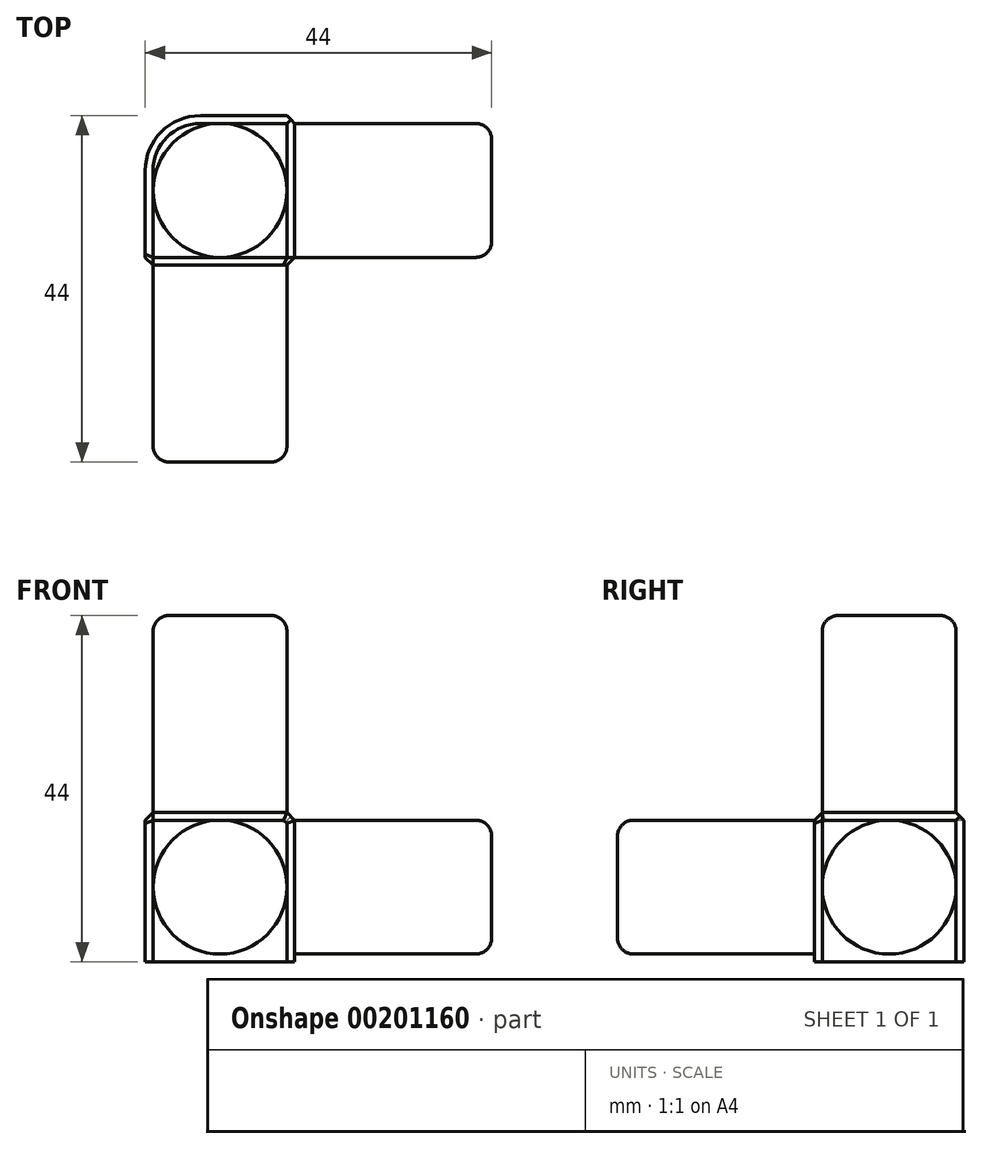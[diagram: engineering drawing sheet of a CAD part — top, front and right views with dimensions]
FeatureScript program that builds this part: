
annotation { "Feature Type Name" : "Feature", "Feature Type Description" : "" }
export const myFeature = defineFeature(function(context is Context, id is Id, definition is map)
    precondition{}
    {
        {
            var Q0;
            Q0=qCreatedBy(makeId("Top.planeOp"),FACE);
            var sketch = newSketch(context, id + "F0", { "sketchPlane" : qUnion([Q0])});
            skLineSegment(sketch, "E0.bottom", {"start": v(-14.38, 5.37) * mm, "end": v(4.62, 5.37) * mm});
            skLineSegment(sketch, "E0.top", {"start": v(-14.38, -13.63) * mm, "end": v(4.62, -13.63) * mm});
            skLineSegment(sketch, "E0.left", {"start": v(-14.38, 5.37) * mm, "end": v(-14.38, -13.63) * mm});
            skLineSegment(sketch, "E0.right", {"start": v(4.62, 5.37) * mm, "end": v(4.62, -13.63) * mm});
            skSolve(sketch);
        }
        {
            var Q0;
            Q0 = qSketchRegion(id + "F0", true);
            extrude(context, id + "F1", {"entities" : qUnion([Q0]), "depth" : 19 * mm});
        }
        {
            var Q0;
            Q0=makeQuery(id+"F1.opExtrude","SWEPT_FACE",FACE,{"disambiguationData":[OSD([sQuery(id+"F0.wireOp",EDGE,"E0.top")])]});
            var sketch = newSketch(context, id + "F2", { "sketchPlane" : qUnion([Q0])});
            skCircle(sketch, "E1", {"center": v(-4.88, 9.5) * mm, "radius": 8.5 * mm});
            skPoint(sketch, "E1.centerSnap0", {"position": v(4.62, 9.5) * mm});
            skPoint(sketch, "E1.centerSnap1", {"position": v(-4.88, 0) * mm});
            skSolve(sketch);
        }
        {
            var Q0;
            Q0=makeQuery(id+"F1.opExtrude","SWEPT_FACE",FACE,{"disambiguationData":[OSD([sQuery(id+"F0.wireOp",EDGE,"E0.right")])]});
            var sketch = newSketch(context, id + "F3", { "sketchPlane" : qUnion([Q0])});
            skCircle(sketch, "E2", {"center": v(-4.13, 9.5) * mm, "radius": 8.5 * mm});
            skPoint(sketch, "E2.centerSnap0", {"position": v(5.37, 9.5) * mm});
            skPoint(sketch, "E2.centerSnap1", {"position": v(-4.13, 0) * mm});
            skSolve(sketch);
        }
        {
            var Q0;
            Q0=makeQuery(id+"F1.opExtrude","CAP_FACE",FACE,{"disambiguationData":[OSD([sQuery(id+"F0.wireOp",EDGE,"E0.bottom"),sQuery(id+"F0.wireOp",EDGE,"E0.top"),sQuery(id+"F0.wireOp",EDGE,"E0.left"),sQuery(id+"F0.wireOp",EDGE,"E0.right")])],"isStart":false});
            var sketch = newSketch(context, id + "F4", { "sketchPlane" : qUnion([Q0])});
            skCircle(sketch, "E3", {"center": v(-4.88, -4.13) * mm, "radius": 8.5 * mm});
            skPoint(sketch, "E3.centerSnap0", {"position": v(-4.88, -13.63) * mm});
            skPoint(sketch, "E3.centerSnap1", {"position": v(-14.38, -4.13) * mm});
            skSolve(sketch);
        }
        {
            var Q0;
            Q0=makeQuery(id+"F2.imprint","IMPRINT",FACE,{"disambiguationData":[TD([[makeQuery(id+"F2.imprint","IMPRINT",EDGE,{"derivedFrom":sQuery(id+"F2.wireOp",EDGE,"E1")}),1.0]])]});
            extrude(context, id + "F5", {"entities" : qUnion([Q0]), "operationType" : NewBodyOperationType.ADD, "depth" : 25 * mm});
        }
        {
            var Q0;
            Q0=makeQuery(id+"F3.imprint","IMPRINT",FACE,{"disambiguationData":[TD([[makeQuery(id+"F3.imprint","IMPRINT",EDGE,{"derivedFrom":sQuery(id+"F3.wireOp",EDGE,"E2")}),1.0]])]});
            extrude(context, id + "F6", {"entities" : qUnion([Q0]), "operationType" : NewBodyOperationType.ADD, "depth" : 25 * mm});
        }
        {
            var Q0;
            Q0=makeQuery(id+"F4.imprint","IMPRINT",FACE,{"disambiguationData":[TD([[makeQuery(id+"F4.imprint","IMPRINT",EDGE,{"derivedFrom":sQuery(id+"F4.wireOp",EDGE,"E3")}),1.0]])]});
            extrude(context, id + "F7", {"entities" : qUnion([Q0]), "operationType" : NewBodyOperationType.ADD, "depth" : 25 * mm});
        }
        {
            var Q0;
            Q0=makeQuery(id+"F5.opExtrude","CAP_EDGE",EDGE,{"disambiguationData":[OSD([sQuery(id+"F2.wireOp",EDGE,"E1")])],"isStart":false});
            var Q1;
            Q1=makeQuery(id+"F6.opExtrude","CAP_EDGE",EDGE,{"disambiguationData":[OSD([sQuery(id+"F3.wireOp",EDGE,"E2")])],"isStart":false});
            var Q2;
            Q2=makeQuery(id+"F7.opExtrude","CAP_EDGE",EDGE,{"disambiguationData":[OSD([sQuery(id+"F4.wireOp",EDGE,"E3")])],"isStart":false});
            fillet(context, id + "F8", {"entities" : qUnion([Q0, Q1, Q2]), "radius" : 2 * mm, "tangentPropagation" : true, "allowEdgeOverflow" : false});
        }
        {
            var Q0;
            Q0=makeQuery(id+"F1.opExtrude","SWEPT_EDGE",EDGE,{"disambiguationData":[OSD([sQuery(id+"F0.wireOp",EDGE,"E0.bottom"),sQuery(id+"F0.wireOp",EDGE,"E0.left")])]});
            fillet(context, id + "F9", {"entities" : qUnion([Q0]), "radius" : 7 * mm, "tangentPropagation" : true, "allowEdgeOverflow" : false});
        }
        {
            var Q0;
            Q0=makeQuery(id+"F1.opExtrude","CAP_EDGE",EDGE,{"disambiguationData":[OSD([sQuery(id+"F0.wireOp",EDGE,"E0.right")])],"isStart":false});
            chamfer(context, id + "F10", {"entities" : qUnion([Q0]), "width" : 1 * mm, "tangentPropagation" : true});
        }
        {
            var Q0;
            Q0=makeQuery(id+"F1.opExtrude","SWEPT_EDGE",EDGE,{"disambiguationData":[OSD([sQuery(id+"F0.wireOp",EDGE,"E0.top"),sQuery(id+"F0.wireOp",EDGE,"E0.right")])]});
            var Q1;
            Q1=makeQuery(id+"F10.opChamfer","BLEND_EDGE",EDGE,{"blendedFrom":[makeQuery(id+"F1.opExtrude","CAP_EDGE",EDGE,{"disambiguationData":[OSD([sQuery(id+"F0.wireOp",EDGE,"E0.right")])],"isStart":false}),makeQuery(id+"F1.opExtrude","SWEPT_FACE",FACE,{"disambiguationData":[OSD([sQuery(id+"F0.wireOp",EDGE,"E0.top")])]})],"blendedInto":[makeQuery(id+"F1.opExtrude","SWEPT_FACE",FACE,{"disambiguationData":[OSD([sQuery(id+"F0.wireOp",EDGE,"E0.top")])]})]});
            var Q2;
            Q2=makeQuery(id+"F1.opExtrude","CAP_EDGE",EDGE,{"disambiguationData":[OSD([sQuery(id+"F0.wireOp",EDGE,"E0.top")])],"isStart":false});
            chamfer(context, id + "F11", {"entities" : qUnion([Q0, Q1, Q2]), "width" : 1 * mm, "tangentPropagation" : true});
        }
        {
            var Q0;
            Q0=makeQuery(id+"F1.opExtrude","CAP_EDGE",EDGE,{"disambiguationData":[OSD([sQuery(id+"F0.wireOp",EDGE,"E0.bottom")])],"isStart":false});
            var Q1;
            {var subQ0=sQuery(id+"F0.wireOp",EDGE,"E0.left");var subQ1=sQuery(id+"F0.wireOp",EDGE,"E0.bottom");Q1=makeQuery(id+"F9.opFillet","BLEND_EDGE",EDGE,{"blendedFrom":[makeQuery(id+"F1.opExtrude","SWEPT_EDGE",EDGE,{"disambiguationData":[OSD([subQ1,subQ0])]}),makeQuery(id+"F1.opExtrude","CAP_FACE",FACE,{"disambiguationData":[OSD([subQ1,sQuery(id+"F0.wireOp",EDGE,"E0.top"),subQ0,sQuery(id+"F0.wireOp",EDGE,"E0.right")])],"isStart":false})],"blendedInto":[makeQuery(id+"F1.opExtrude","CAP_FACE",FACE,{"disambiguationData":[OSD([subQ1,sQuery(id+"F0.wireOp",EDGE,"E0.top"),subQ0,sQuery(id+"F0.wireOp",EDGE,"E0.right")])],"isStart":false})]});}
            var Q2;
            Q2=makeQuery(id+"F1.opExtrude","CAP_EDGE",EDGE,{"disambiguationData":[OSD([sQuery(id+"F0.wireOp",EDGE,"E0.left")])],"isStart":false});
            var Q3;
            Q3=makeQuery(id+"F1.opExtrude","SWEPT_EDGE",EDGE,{"disambiguationData":[OSD([sQuery(id+"F0.wireOp",EDGE,"E0.bottom"),sQuery(id+"F0.wireOp",EDGE,"E0.right")])]});
            var Q4;
            Q4=makeQuery(id+"F1.opExtrude","SWEPT_EDGE",EDGE,{"disambiguationData":[OSD([sQuery(id+"F0.wireOp",EDGE,"E0.top"),sQuery(id+"F0.wireOp",EDGE,"E0.left")])]});
            var Q5;
            Q5=makeQuery(id+"F11.opChamfer","BLEND_EDGE",EDGE,{"blendedFrom":[makeQuery(id+"F1.opExtrude","CAP_EDGE",EDGE,{"disambiguationData":[OSD([sQuery(id+"F0.wireOp",EDGE,"E0.top")])],"isStart":false}),makeQuery(id+"F1.opExtrude","SWEPT_FACE",FACE,{"disambiguationData":[OSD([sQuery(id+"F0.wireOp",EDGE,"E0.left")])]})],"blendedInto":[makeQuery(id+"F1.opExtrude","SWEPT_FACE",FACE,{"disambiguationData":[OSD([sQuery(id+"F0.wireOp",EDGE,"E0.left")])]})]});
            chamfer(context, id + "F12", {"entities" : qUnion([Q0, Q1, Q2, Q3, Q4, Q5]), "width" : 1 * mm, "tangentPropagation" : true});
        }
    });
